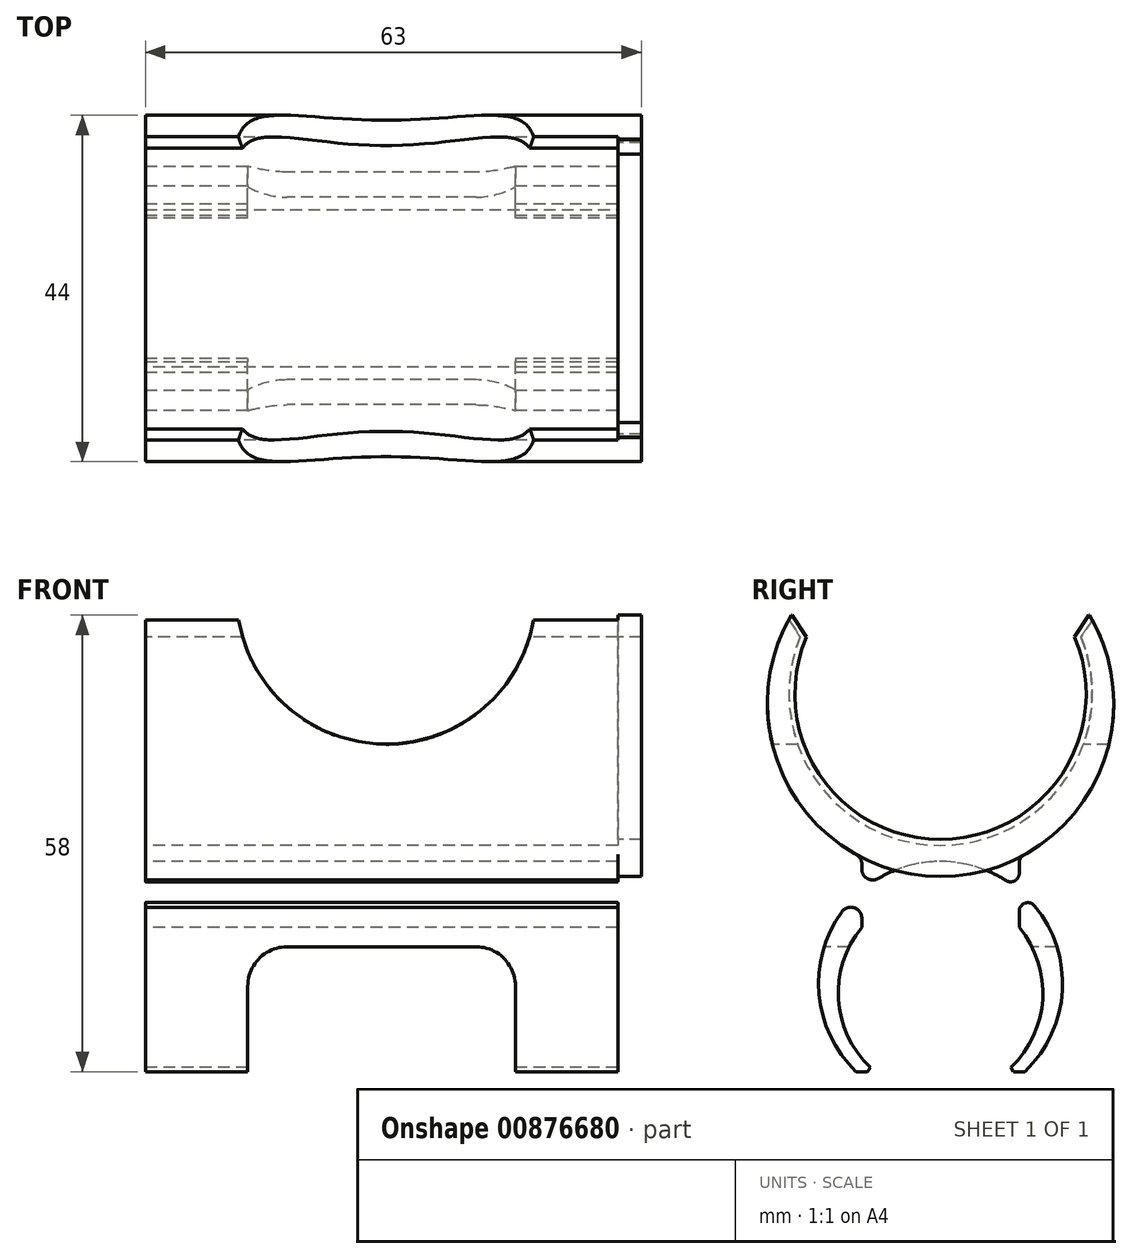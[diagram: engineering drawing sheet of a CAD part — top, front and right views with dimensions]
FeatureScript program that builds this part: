
annotation { "Feature Type Name" : "Feature", "Feature Type Description" : "" }
export const myFeature = defineFeature(function(context is Context, id is Id, definition is map)
    precondition{}
    {
        {
            var Q0;
            Q0=qCreatedBy(makeId("Right.planeOp"),FACE);
            var sketch = newSketch(context, id + "F0", { "sketchPlane" : qUnion([Q0])});
            skCircle(sketch, "E0", {"center": v(0, 0) * mm, "radius": 19.25 * mm});
            skCircle(sketch, "E1", {"center": v(0, -1.2) * mm, "radius": 22 * mm});
            skLineSegment(sketch, "E2.bottom", {"start": v(10, -34) * mm, "end": v(-10, -34) * mm});
            skLineSegment(sketch, "E2.top", {"start": v(10, -20) * mm, "end": v(-10, -20) * mm});
            skLineSegment(sketch, "E2.left", {"start": v(10, -34) * mm, "end": v(10, -20) * mm});
            skLineSegment(sketch, "E2.right", {"start": v(-10, -34) * mm, "end": v(-10, -20) * mm});
            skPoint(sketch, "E2.middle", {"position": v(0, -27) * mm});
            skCircle(sketch, "E3", {"center": v(0, -38) * mm, "radius": 13 * mm});
            skCircle(sketch, "E4", {"center": v(0, -36.8) * mm, "radius": 15.5 * mm});
            skSolve(sketch);
        }
        {
            var Q0;
            Q0=makeQuery(id+"F0.imprint","IMPRINT",FACE,{"disambiguationData":[TD([[makeQuery(id+"F0.imprint","IMPRINT",EDGE,{"derivedFrom":sQuery(id+"F0.wireOp",EDGE,"E0")}),-1.0]])]});
            var Q1;
            {var subQ0=sQuery(id+"F0.wireOp",EDGE,"E4");var subQ1=sQuery(id+"F0.wireOp",EDGE,"E2.left");var subQ2=makeQuery(id+"F0.imprint","INTERSECT",VERTEX,{"derivedFrom":[subQ1,subQ0]});Q1=makeQuery(id+"F0.imprint","IMPRINT",FACE,{"disambiguationData":[TD([[makeQuery(id+"F0.imprint","IMPRINT",EDGE,{"disambiguationData":[TD([[subQ2,1.0]])],"derivedFrom":subQ1}),-1.0]])]});}
            var Q2;
            {var subQ0=sQuery(id+"F0.wireOp",EDGE,"E4");var subQ1=sQuery(id+"F0.wireOp",EDGE,"E1");var subQ2=makeQuery(id+"F0.imprint","INTERSECT",VERTEX,{"disambiguationData":[OD(0.0)],"derivedFrom":[subQ1,subQ0]});Q2=makeQuery(id+"F0.imprint","IMPRINT",FACE,{"disambiguationData":[TD([[makeQuery(id+"F0.imprint","IMPRINT",EDGE,{"disambiguationData":[TD([[subQ2,-1.0]])],"derivedFrom":subQ1}),1.0]])]});}
            var Q3;
            {var subQ5=sQuery(id+"F0.wireOp",EDGE,"E4");var subQ8=sQuery(id+"F0.wireOp",EDGE,"E1");var subQ9=makeQuery(id+"F0.imprint","INTERSECT",VERTEX,{"disambiguationData":[OD(0.0)],"derivedFrom":[subQ8,subQ5]});Q3=makeQuery(id+"F0.imprint","IMPRINT",FACE,{"disambiguationData":[TD([[makeQuery(id+"F0.imprint","IMPRINT",EDGE,{"disambiguationData":[TD([[subQ9,-1.0]])],"derivedFrom":subQ8}),-1.0]])]});}
            var Q4;
            {var subQ0=sQuery(id+"F0.wireOp",EDGE,"E2.right");var subQ1=sQuery(id+"F0.wireOp",EDGE,"E1");var subQ2=makeQuery(id+"F0.imprint","INTERSECT",VERTEX,{"derivedFrom":[subQ1,subQ0]});Q4=makeQuery(id+"F0.imprint","IMPRINT",FACE,{"disambiguationData":[TD([[makeQuery(id+"F0.imprint","IMPRINT",EDGE,{"disambiguationData":[TD([[subQ2,-1.0]])],"derivedFrom":subQ1}),-1.0]])]});}
            var Q5;
            {var subQ0=sQuery(id+"F0.wireOp",EDGE,"E2.left");var subQ1=sQuery(id+"F0.wireOp",EDGE,"E1");var subQ2=makeQuery(id+"F0.imprint","INTERSECT",VERTEX,{"derivedFrom":[subQ1,subQ0]});Q5=makeQuery(id+"F0.imprint","IMPRINT",FACE,{"disambiguationData":[TD([[makeQuery(id+"F0.imprint","IMPRINT",EDGE,{"disambiguationData":[TD([[subQ2,1.0]])],"derivedFrom":subQ1}),-1.0]])]});}
            var Q6;
            {var subQ1=sQuery(id+"F0.wireOp",EDGE,"E2.top");Q6=makeQuery(id+"F0.imprint","IMPRINT",FACE,{"disambiguationData":[TD([[makeQuery(id+"F0.imprint","IMPRINT",EDGE,{"derivedFrom":subQ1}),1.0]])]});}
            extrude(context, id + "F1", {"entities" : qUnion([Q0, Q1, Q2, Q3, Q4, Q5, Q6]), "depth" : 60 * mm, "offsetDistance" : 25 * mm});
        }
        {
            var Q0;
            Q0=makeQuery(id+"F1.opExtrude","CAP_FACE",FACE,{"disambiguationData":[OSD([sQuery(id+"F0.wireOp",EDGE,"E0"),sQuery(id+"F0.wireOp",EDGE,"E1"),sQuery(id+"F0.wireOp",EDGE,"E2.left"),sQuery(id+"F0.wireOp",EDGE,"E2.right"),sQuery(id+"F0.wireOp",EDGE,"E3"),sQuery(id+"F0.wireOp",EDGE,"E4")])],"isStart":false});
            var sketch = newSketch(context, id + "F2", { "sketchPlane" : qUnion([Q0])});
            skCircle(sketch, "E5", {"center": v(0, 0) * mm, "radius": 18.5 * mm});
            skCircle(sketch, "E6", {"center": v(0, -1.2) * mm, "radius": 22 * mm});
            skSolve(sketch);
        }
        {
            var Q0;
            Q0 = qSketchRegion(id + "F2", true);
            extrude(context, id + "F3", {"entities" : qUnion([Q0]), "operationType" : NewBodyOperationType.ADD, "depth" : 3 * mm, "offsetDistance" : 25 * mm});
        }
        {
            var Q0;
            Q0=makeQuery(id+"F3.opExtrude","CAP_FACE",FACE,{"disambiguationData":[OSD([sQuery(id+"F2.wireOp",EDGE,"E5"),sQuery(id+"F2.wireOp",EDGE,"E6")])],"isStart":false});
            var sketch = newSketch(context, id + "F4", { "sketchPlane" : qUnion([Q0])});
            skLineSegment(sketch, "E7.bottom", {"start": v(-25, 10) * mm, "end": v(25, 10) * mm});
            skLineSegment(sketch, "E7.top", {"start": v(-25, 35) * mm, "end": v(25, 35) * mm});
            skLineSegment(sketch, "E7.left", {"start": v(-25, 10) * mm, "end": v(-25, 35) * mm});
            skLineSegment(sketch, "E7.right", {"start": v(25, 10) * mm, "end": v(25, 35) * mm});
            skLineSegment(sketch, "E8.bottom", {"start": v(68.01, -85.05) * mm, "end": v(-68.01, -85.05) * mm});
            skLineSegment(sketch, "E8.top", {"start": v(68.01, -48) * mm, "end": v(-68.01, -48) * mm});
            skLineSegment(sketch, "E8.left", {"start": v(68.01, -85.05) * mm, "end": v(68.01, -48) * mm});
            skLineSegment(sketch, "E8.right", {"start": v(-68.01, -85.05) * mm, "end": v(-68.01, -48) * mm});
            skPoint(sketch, "E8.middle", {"position": v(0, -66.53) * mm});
            skSolve(sketch);
        }
        {
            var Q0;
            Q0 = qSketchRegion(id + "F4", true);
            extrude(context, id + "F5", {"entities" : qUnion([Q0]), "operationType" : NewBodyOperationType.REMOVE, "endBound" : BoundingType.THROUGH_ALL, "oppositeDirection" : true, "depth" : 25 * mm, "offsetDistance" : 25 * mm});
        }
        {
            var Q0;
            Q0=makeQuery(id+"F5.boolean.opBoolean","INTERSECT",EDGE,{"disambiguationData":[OD(1.0)],"derivedFrom":[makeQuery(id+"F1.opExtrude","SWEPT_FACE",FACE,{"disambiguationData":[OSD([sQuery(id+"F0.wireOp",EDGE,"E0")])]}),makeQuery(id+"F5.opExtrude","SWEPT_FACE",FACE,{"disambiguationData":[OSD([sQuery(id+"F4.wireOp",EDGE,"E7.bottom")])]})]});
            var Q1;
            Q1=makeQuery(id+"F5.boolean.opBoolean","INTERSECT",EDGE,{"disambiguationData":[OD(0.0)],"derivedFrom":[makeQuery(id+"F1.opExtrude","SWEPT_FACE",FACE,{"disambiguationData":[OSD([sQuery(id+"F0.wireOp",EDGE,"E0")])]}),makeQuery(id+"F5.opExtrude","SWEPT_FACE",FACE,{"disambiguationData":[OSD([sQuery(id+"F4.wireOp",EDGE,"E7.bottom")])]})]});
            chamfer(context, id + "F6", {"entities" : qUnion([Q0, Q1]), "width" : 2 * mm, "tangentPropagation" : true});
        }
        {
            var Q0;
            Q0=makeQuery(id+"F5.boolean.opBoolean","INTERSECT",EDGE,{"disambiguationData":[OD(0.0)],"derivedFrom":[makeQuery(id+"F3.opExtrude","SWEPT_FACE",FACE,{"disambiguationData":[OSD([sQuery(id+"F2.wireOp",EDGE,"E5")])]}),makeQuery(id+"F5.opExtrude","SWEPT_FACE",FACE,{"disambiguationData":[OSD([sQuery(id+"F4.wireOp",EDGE,"E7.bottom")])]})]});
            var Q1;
            Q1=makeQuery(id+"F5.boolean.opBoolean","INTERSECT",EDGE,{"disambiguationData":[OD(1.0)],"derivedFrom":[makeQuery(id+"F3.opExtrude","SWEPT_FACE",FACE,{"disambiguationData":[OSD([sQuery(id+"F2.wireOp",EDGE,"E5")])]}),makeQuery(id+"F5.opExtrude","SWEPT_FACE",FACE,{"disambiguationData":[OSD([sQuery(id+"F4.wireOp",EDGE,"E7.bottom")])]})]});
            chamfer(context, id + "F7", {"entities" : qUnion([Q0, Q1]), "width" : 2 * mm, "tangentPropagation" : true});
        }
        {
            var Q0;
            Q0=makeQuery(id+"F5.boolean.opBoolean","INTERSECT",EDGE,{"disambiguationData":[OD(0.0)],"derivedFrom":[makeQuery(id+"F1.opExtrude","SWEPT_FACE",FACE,{"disambiguationData":[OSD([sQuery(id+"F0.wireOp",EDGE,"E3")])]}),makeQuery(id+"F5.opExtrude","SWEPT_FACE",FACE,{"disambiguationData":[OSD([sQuery(id+"F4.wireOp",EDGE,"E8.top")])]})]});
            var Q1;
            Q1=makeQuery(id+"F5.boolean.opBoolean","INTERSECT",EDGE,{"disambiguationData":[OD(1.0)],"derivedFrom":[makeQuery(id+"F1.opExtrude","SWEPT_FACE",FACE,{"disambiguationData":[OSD([sQuery(id+"F0.wireOp",EDGE,"E3")])]}),makeQuery(id+"F5.opExtrude","SWEPT_FACE",FACE,{"disambiguationData":[OSD([sQuery(id+"F4.wireOp",EDGE,"E8.top")])]})]});
            chamfer(context, id + "F8", {"entities" : qUnion([Q0, Q1]), "chamferType" : ChamferType.OFFSET_ANGLE, "width" : 1 * mm, "oppositeDirection" : false, "angle" : 60 * degree, "tangentPropagation" : true});
        }
        {
            var Q0;
            Q0=makeQuery(id+"F1.opExtrude","SWEPT_EDGE",EDGE,{"disambiguationData":[OSD([sQuery(id+"F0.wireOp",EDGE,"E1"),sQuery(id+"F0.wireOp",EDGE,"E2.right")])]});
            var Q1;
            Q1=makeQuery(id+"F1.opExtrude","SWEPT_EDGE",EDGE,{"disambiguationData":[OSD([sQuery(id+"F0.wireOp",EDGE,"E2.right"),sQuery(id+"F0.wireOp",EDGE,"E4")])]});
            fillet(context, id + "F9", {"entities" : qUnion([Q0, Q1]), "radius" : 1.4 * mm, "tangentPropagation" : true, "allowEdgeOverflow" : false});
        }
        {
            var Q0;
            Q0=makeQuery(id+"F1.opExtrude","SWEPT_EDGE",EDGE,{"disambiguationData":[OSD([sQuery(id+"F0.wireOp",EDGE,"E1"),sQuery(id+"F0.wireOp",EDGE,"E2.left")])]});
            var Q1;
            Q1=makeQuery(id+"F1.opExtrude","SWEPT_EDGE",EDGE,{"disambiguationData":[OSD([sQuery(id+"F0.wireOp",EDGE,"E2.left"),sQuery(id+"F0.wireOp",EDGE,"E4")])]});
            fillet(context, id + "F10", {"entities" : qUnion([Q0, Q1]), "radius" : 1.1 * mm, "tangentPropagation" : true, "allowEdgeOverflow" : false});
        }
        {
            var Q0;
            Q0=qCreatedBy(makeId("Front.planeOp"),FACE);
            cPlane(context, id + "F12", {"entities" : qUnion([Q0]), "cplaneType" : CPlaneType.OFFSET, "offset" : 22 * mm, "width" : 150 * mm, "height" : 150 * mm});
        }
        {
            var Q0;
            Q0=qCreatedBy(id+"F12.planeOp",FACE);
            var sketch = newSketch(context, id + "F13", { "sketchPlane" : qUnion([Q0])});
            skCircle(sketch, "E9", {"center": v(30.57, 12.6) * mm, "radius": 19 * mm});
            skSolve(sketch);
        }
        {
            var Q0;
            Q0 = qSketchRegion(id + "F13", true);
            extrude(context, id + "F14", {"entities" : qUnion([Q0]), "operationType" : NewBodyOperationType.REMOVE, "endBound" : BoundingType.THROUGH_ALL, "oppositeDirection" : true, "depth" : 25 * mm, "offsetDistance" : 25 * mm});
        }
        {
            var Q0;
            Q0=qCreatedBy(id+"F12.planeOp",FACE);
            var sketch = newSketch(context, id + "F15", { "sketchPlane" : qUnion([Q0])});
            skLineSegment(sketch, "E10.bottom", {"start": v(47, -58.14) * mm, "end": v(13, -58.14) * mm});
            skLineSegment(sketch, "E10.top", {"start": v(47, -32.14) * mm, "end": v(13, -32.14) * mm});
            skLineSegment(sketch, "E10.left", {"start": v(47, -58.14) * mm, "end": v(47, -32.14) * mm});
            skLineSegment(sketch, "E10.right", {"start": v(13, -58.14) * mm, "end": v(13, -32.14) * mm});
            skPoint(sketch, "E10.middle", {"position": v(30, -45.14) * mm});
            skSolve(sketch);
        }
        {
            var Q0;
            Q0 = qSketchRegion(id + "F15", true);
            extrude(context, id + "F16", {"entities" : qUnion([Q0]), "operationType" : NewBodyOperationType.REMOVE, "endBound" : BoundingType.THROUGH_ALL, "oppositeDirection" : true, "depth" : 25 * mm, "offsetDistance" : 25 * mm});
        }
        {
            var Q0;
            Q0=makeQuery(id+"F16.boolean.opBoolean","COPY",EDGE,{"disambiguationData":[OD(0.0)],"derivedFrom":makeQuery(id+"F16.opExtrude","SWEPT_EDGE",EDGE,{"disambiguationData":[OSD([sQuery(id+"F15.wireOp",EDGE,"E10.top"),sQuery(id+"F15.wireOp",EDGE,"E10.right")])]})});
            var Q1;
            Q1=makeQuery(id+"F16.boolean.opBoolean","COPY",EDGE,{"disambiguationData":[OD(1.0)],"derivedFrom":makeQuery(id+"F16.opExtrude","SWEPT_EDGE",EDGE,{"disambiguationData":[OSD([sQuery(id+"F15.wireOp",EDGE,"E10.top"),sQuery(id+"F15.wireOp",EDGE,"E10.right")])]})});
            var Q2;
            Q2=makeQuery(id+"F16.boolean.opBoolean","COPY",EDGE,{"disambiguationData":[OD(0.0)],"derivedFrom":makeQuery(id+"F16.opExtrude","SWEPT_EDGE",EDGE,{"disambiguationData":[OSD([sQuery(id+"F15.wireOp",EDGE,"E10.top"),sQuery(id+"F15.wireOp",EDGE,"E10.left")])]})});
            var Q3;
            Q3=makeQuery(id+"F16.boolean.opBoolean","COPY",EDGE,{"disambiguationData":[OD(1.0)],"derivedFrom":makeQuery(id+"F16.opExtrude","SWEPT_EDGE",EDGE,{"disambiguationData":[OSD([sQuery(id+"F15.wireOp",EDGE,"E10.top"),sQuery(id+"F15.wireOp",EDGE,"E10.left")])]})});
            fillet(context, id + "F17", {"entities" : qUnion([Q0, Q1, Q2, Q3]), "radius" : 5 * mm, "tangentPropagation" : true, "allowEdgeOverflow" : false});
        }
    });
